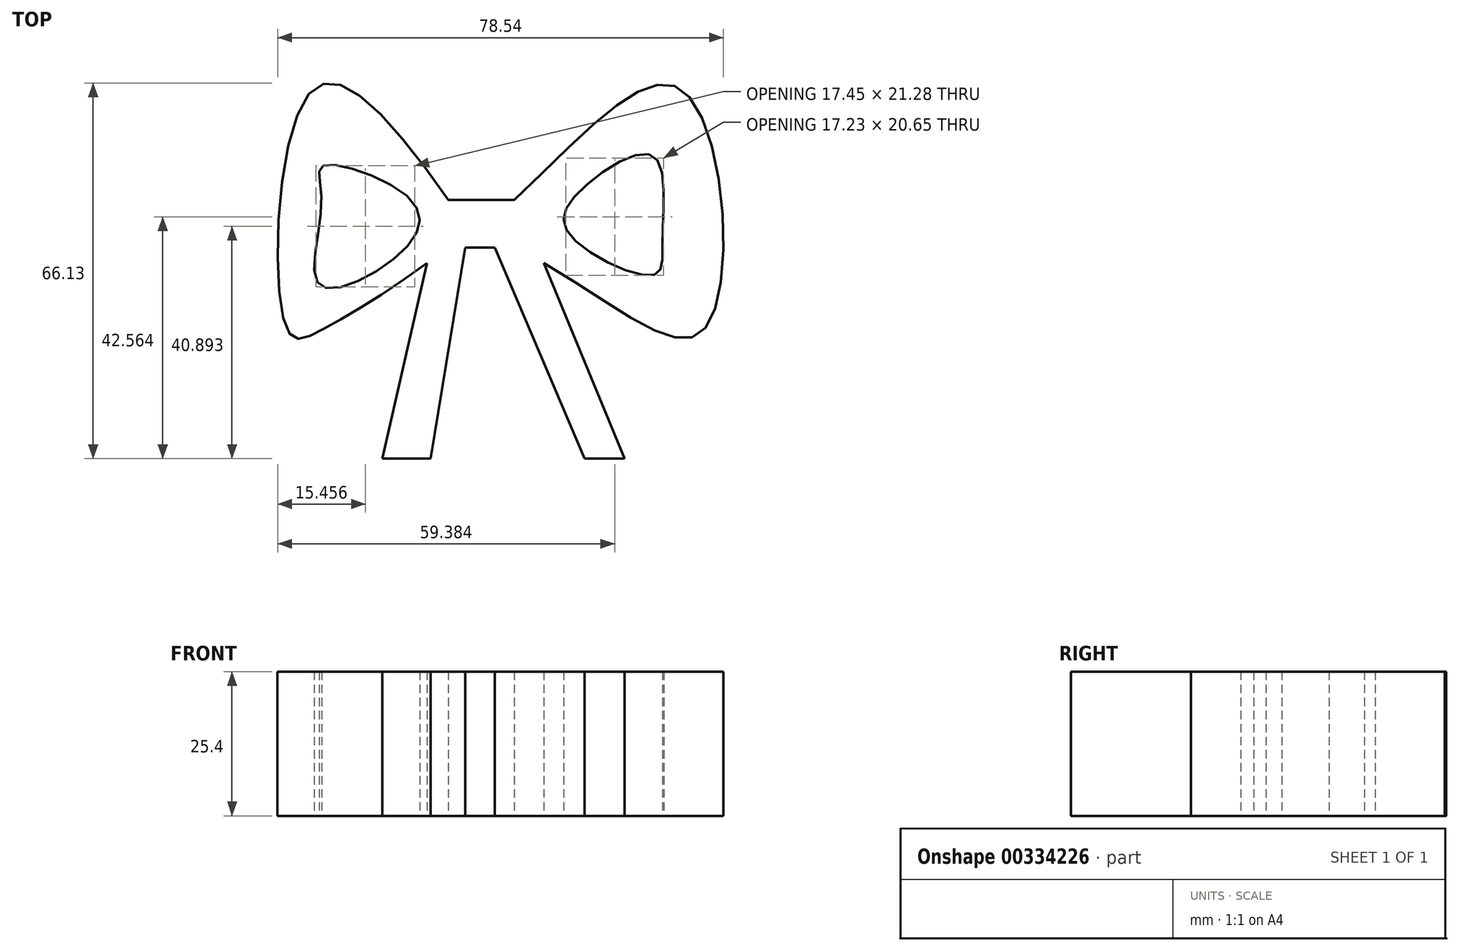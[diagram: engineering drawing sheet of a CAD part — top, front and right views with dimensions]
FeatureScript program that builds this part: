
annotation { "Feature Type Name" : "Feature", "Feature Type Description" : "" }
export const myFeature = defineFeature(function(context is Context, id is Id, definition is map)
    precondition{}
    {
        {
            var Q0;
            Q0=qCreatedBy(makeId("Top.planeOp"),FACE);
            var sketch = newSketch(context, id + "F0", { "sketchPlane" : qUnion([Q0])});
            skLineSegment(sketch, "E0.bottom", {"start": v(-2.96, 6.34) * mm, "end": v(8.66, 6.34) * mm});
            skLineSegment(sketch, "E0.top", {"start": v(-2.96, -2.02) * mm, "end": v(8.66, -2.02) * mm});
            skLineSegment(sketch, "E0.left", {"start": v(-2.96, 6.34) * mm, "end": v(-2.96, -2.02) * mm});
            skLineSegment(sketch, "E0.right", {"start": v(8.66, 6.34) * mm, "end": v(8.66, -2.02) * mm});
            skFitSpline(sketch, "E1", {"points": [v(8.66, 6.34) * mm, v(38.8, 25.19) * mm, v(42.17, -16.34) * mm, v(8.66, -2.02) * mm], "startDerivative": vector(118.83, 112.5) * mm, "endDerivative": vector(-146.83, 72.92) * mm});
            skFitSpline(sketch, "E2", {"points": [v(-2.96, 6.34) * mm, v(-27.02, 25.6) * mm, v(-31.28, -16.7) * mm, v(-26.3, -17.08) * mm, v(-2.96, -2.02) * mm], "startDerivative": vector(-96.7, 137.1) * mm, "endDerivative": vector(100.67, 76.26) * mm});
            skLineSegment(sketch, "E3", {"start": v(-6.71, -4.8) * mm, "end": v(-14.61, -39.19) * mm});
            skLineSegment(sketch, "E4", {"start": v(0, -2.02) * mm, "end": v(-6.1, -39.19) * mm});
            skLineSegment(sketch, "E5", {"start": v(-6.1, -39.19) * mm, "end": v(-14.61, -39.19) * mm});
            skLineSegment(sketch, "E6", {"start": v(13.82, -4.8) * mm, "end": v(28.04, -39.19) * mm});
            skLineSegment(sketch, "E7", {"start": v(5.18, -2.02) * mm, "end": v(21.03, -39.19) * mm});
            skLineSegment(sketch, "E8", {"start": v(21.03, -39.19) * mm, "end": v(28.04, -39.19) * mm});
            skFitSpline(sketch, "E9", {"points": [v(-25, 12.34) * mm, v(-25.3, 6.25) * mm, v(-25.6, -8.69) * mm, v(-10.97, -2.6) * mm, v(-9.45, 6.25) * mm, v(-25, 12.34) * mm]});
            skFitSpline(sketch, "E10", {"points": [v(19.2, 6.86) * mm, v(32.92, 14.17) * mm, v(34.75, 0) * mm, v(33.22, -6.86) * mm, v(18.6, 0) * mm, v(19.2, 6.86) * mm]});
            skPoint(sketch, "E11.firstSnap0", {"position": v(2.85, 6.34) * mm});
            skLineSegment(sketch, "E11.right", {"start": v(8.66, 0) * mm, "end": v(8.66, 2.16) * mm});
            skSolve(sketch);
        }
        {
            var Q0;
            {var subQ0=sQuery(id+"F0.wireOp",EDGE,"E0.left");Q0=makeQuery(id+"F0.imprint","IMPRINT",FACE,{"disambiguationData":[TD([[makeQuery(id+"F0.imprint","IMPRINT",EDGE,{"derivedFrom":subQ0}),-1.0]])]});}
            var Q1;
            Q1=makeQuery(id+"F0.imprint","IMPRINT",FACE,{"disambiguationData":[TD([[makeQuery(id+"F0.imprint","IMPRINT",EDGE,{"derivedFrom":sQuery(id+"F0.wireOp",EDGE,"E10")}),1.0]])]});
            var Q2;
            {var subQ7=sQuery(id+"F0.wireOp",EDGE,"E0.bottom");Q2=makeQuery(id+"F0.imprint","IMPRINT",FACE,{"disambiguationData":[TD([[makeQuery(id+"F0.imprint","IMPRINT",EDGE,{"derivedFrom":subQ7}),-1.0]])]});}
            var Q3;
            {var subQ1=sQuery(id+"F0.wireOp",EDGE,"E6");Q3=makeQuery(id+"F0.imprint","IMPRINT",FACE,{"disambiguationData":[TD([[makeQuery(id+"F0.imprint","IMPRINT",EDGE,{"derivedFrom":subQ1}),-1.0]])]});}
            var Q4;
            {var subQ4=sQuery(id+"F0.wireOp",EDGE,"E3");Q4=makeQuery(id+"F0.imprint","IMPRINT",FACE,{"disambiguationData":[TD([[makeQuery(id+"F0.imprint","IMPRINT",EDGE,{"derivedFrom":subQ4}),1.0]])]});}
            extrude(context, id + "F1", {"entities" : qUnion([Q0, Q1, Q2, Q3, Q4]), "depth" : 25.4 * mm});
        }
    });
